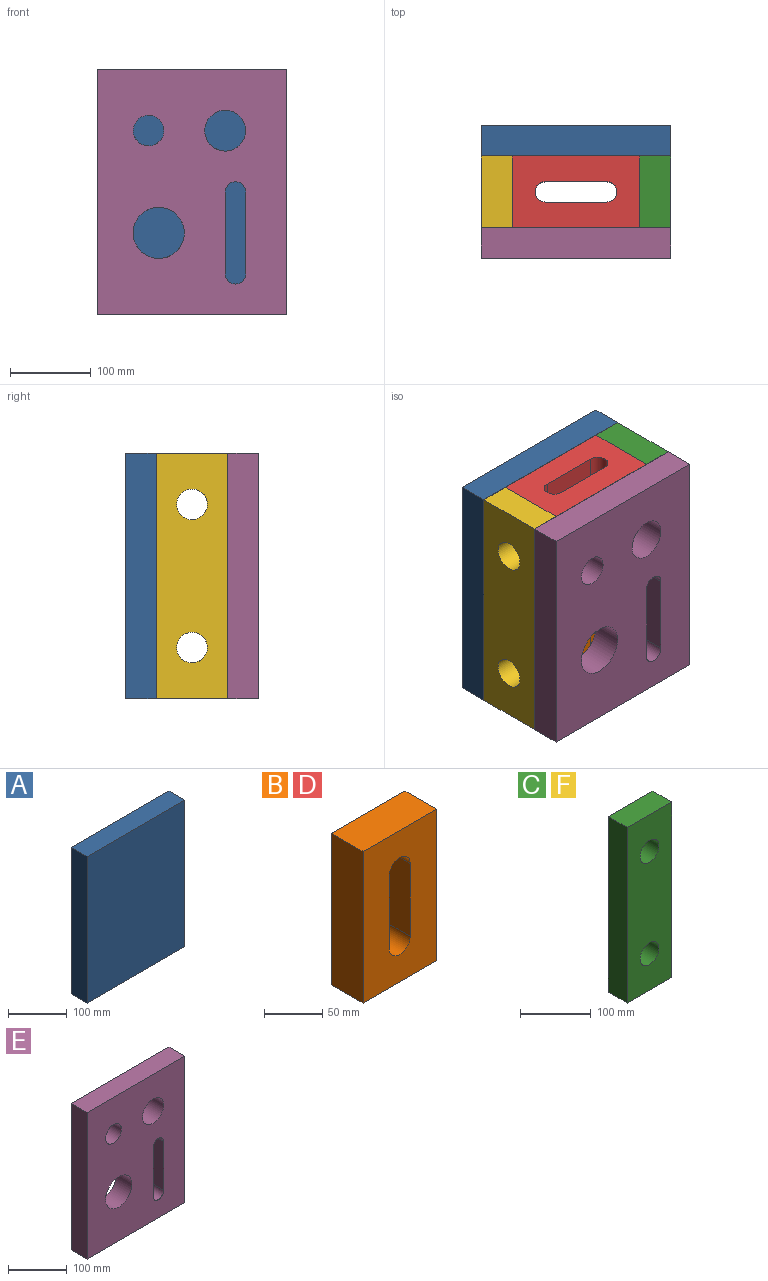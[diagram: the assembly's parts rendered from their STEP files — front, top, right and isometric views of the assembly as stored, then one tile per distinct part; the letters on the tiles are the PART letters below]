
ASSEMBLY  parts=6 mates=4
PART A: 6 faces, bbox 235x38.1x304.8 mm
  f0: plane 304.8x234.95mm, normal (0,-1,0), area 71612.8mm2, adj f1,f3,f4,f5
  f1: plane 304.8x38.1mm, normal (1,0,0), area 11612.9mm2, adj f0,f2,f4,f5
  f2: plane 304.8x234.95mm, normal (0,1,0), area 71612.8mm2, adj f1,f3,f4,f5
  f3: plane 304.8x38.1mm, normal (-1,0,0), area 11612.9mm2, adj f0,f2,f4,f5
  f4: plane 234.95x38.1mm, normal (0,0,1), area 8951.6mm2, adj f0,f1,f2,f3
  f5: plane 234.95x38.1mm, normal (0,0,-1), area 8951.6mm2, adj f0,f1,f2,f3
PART B: 10 faces, bbox 88.9x38.1x158.8 mm
  f0: plane 158.75x38.1mm, normal (-1,0,0), area 6048.4mm2, adj f1,f3,f4,f5
  f1: plane 158.75x88.9mm, normal (0,-1,0), area 11670.7mm2, adj f0,f2,f4,f5,f6,f7,f8,f9
  f2: plane 158.75x38.1mm, normal (1,0,0), area 6048.4mm2, adj f1,f3,f4,f5
  f3: plane 158.75x88.9mm, normal (0,1,0), area 11670.7mm2, adj f0,f2,f4,f5,f6,f7,f8,f9
  f4: plane 88.9x38.1mm, normal (0,0,1), area 3387.1mm2, adj f0,f1,f2,f3
  f5: plane 88.9x38.1mm, normal (0,0,-1), area 3387.1mm2, adj f0,f1,f2,f3
  f6: plane 76.2x38.1mm, normal (-1,0,0), area 2903.2mm2, adj f1,f3,f7,f8
  f7: cylinder r=12.7mm len=38.1mm, axis (0,1,0), area 1520.1mm2, adj f1,f3,f6,f9
  f8: cylinder r=12.7mm len=38.1mm, axis (0,1,0), area 1520.1mm2, adj f1,f3,f6,f9
  f9: plane 76.2x38.1mm, normal (1,0,0), area 2903.2mm2, adj f1,f3,f7,f8
PART C: 8 faces, bbox 88.9x38.1x304.8 mm
  f0: plane 304.8x88.9mm, normal (0,-1,0), area 24816.5mm2, adj f1,f3,f4,f5,f6,f7
  f1: plane 304.8x38.1mm, normal (1,0,0), area 11612.9mm2, adj f0,f2,f4,f5
  f2: plane 304.8x88.9mm, normal (0,1,0), area 24816.5mm2, adj f1,f3,f4,f5,f6,f7
  f3: plane 304.8x38.1mm, normal (-1,0,0), area 11612.9mm2, adj f0,f2,f4,f5
  f4: plane 88.9x38.1mm, normal (0,0,1), area 3387.1mm2, adj f0,f1,f2,f3
  f5: plane 88.9x38.1mm, normal (0,0,-1), area 3387.1mm2, adj f0,f1,f2,f3
  f6: cylinder r=19.05mm len=38.1mm, axis (0,1,0), area 4560.4mm2, adj f0,f2
  f7: cylinder r=19.05mm len=38.1mm, axis (0,1,0), area 4560.4mm2, adj f0,f2
PART D: same geometry as B
PART E: 13 faces, bbox 235x38.1x304.8 mm
  f0: plane 304.8x234.95mm, normal (0,-1,0), area 62191.6mm2, adj f2,f3,f4,f5,f6,f7,f8,f9
  f1: plane 304.8x234.95mm, normal (0,1,0), area 62191.6mm2, adj f2,f3,f4,f5,f6,f7,f8,f9
  f2: plane 304.8x38.1mm, normal (1,0,0), area 11612.9mm2, adj f0,f1,f4,f5
  f3: plane 304.8x38.1mm, normal (-1,0,0), area 11612.9mm2, adj f0,f1,f4,f5
  f4: plane 234.95x38.1mm, normal (0,0,1), area 8951.6mm2, adj f0,f1,f2,f3
  f5: plane 234.95x38.1mm, normal (0,0,-1), area 8951.6mm2, adj f0,f1,f2,f3
  f6: cylinder r=25.4mm len=50.8mm, axis (0,1,0), area 6080.5mm2, adj f0,f1
  f7: cylinder r=19.05mm len=38.1mm, axis (0,1,0), area 4560.4mm2, adj f0,f1
  f8: cylinder r=31.75mm len=63.5mm, axis (0,1,0), area 7600.6mm2, adj f0,f1
  f9: plane 101.6x38.1mm, normal (-1,0,0), area 3871mm2, adj f0,f1,f10,f11
  f10: cylinder r=12.7mm len=38.1mm, axis (0,1,0), area 1520.1mm2, adj f0,f1,f9,f12
  f11: cylinder r=12.7mm len=38.1mm, axis (0,1,0), area 1520.1mm2, adj f0,f1,f9,f12
  f12: plane 101.6x38.1mm, normal (1,0,0), area 3871mm2, adj f0,f1,f10,f11
PART F: same geometry as C
PLACE A t=(349.8,116.47,-160.36)mm
PLACE B rot(axis=(-0.58,0.58,-0.58),120deg) t=(-132.8,141.87,-122.26)mm
PLACE C rot(axis=(0,0,-1),90deg) t=(25.95,-518.53,-160.36)mm
PLACE D rot(axis=(-0.58,0.58,-0.58),120deg) t=(-132.8,141.87,144.44)mm
PLACE E t=(89.45,-10.53,-160.36)mm fixed
PLACE F rot(axis=(0,0,-1),90deg) t=(-170.9,-518.53,-160.36)mm
MATE fastened B.f0 <-> A.f0  axis (0,1,0) through (-53.42,116.47,-160.36)mm
MATE fastened F.f3 <-> A.f0  axis (0,1,0) through (-170.9,116.47,-7.96)mm
MATE fastened E.f1 <-> C.f1  axis (0,1,0) through (64.05,27.57,-7.96)mm
MATE fastened E.f1 <-> D.f2  axis (0,1,0) through (-53.42,27.57,144.44)mm
